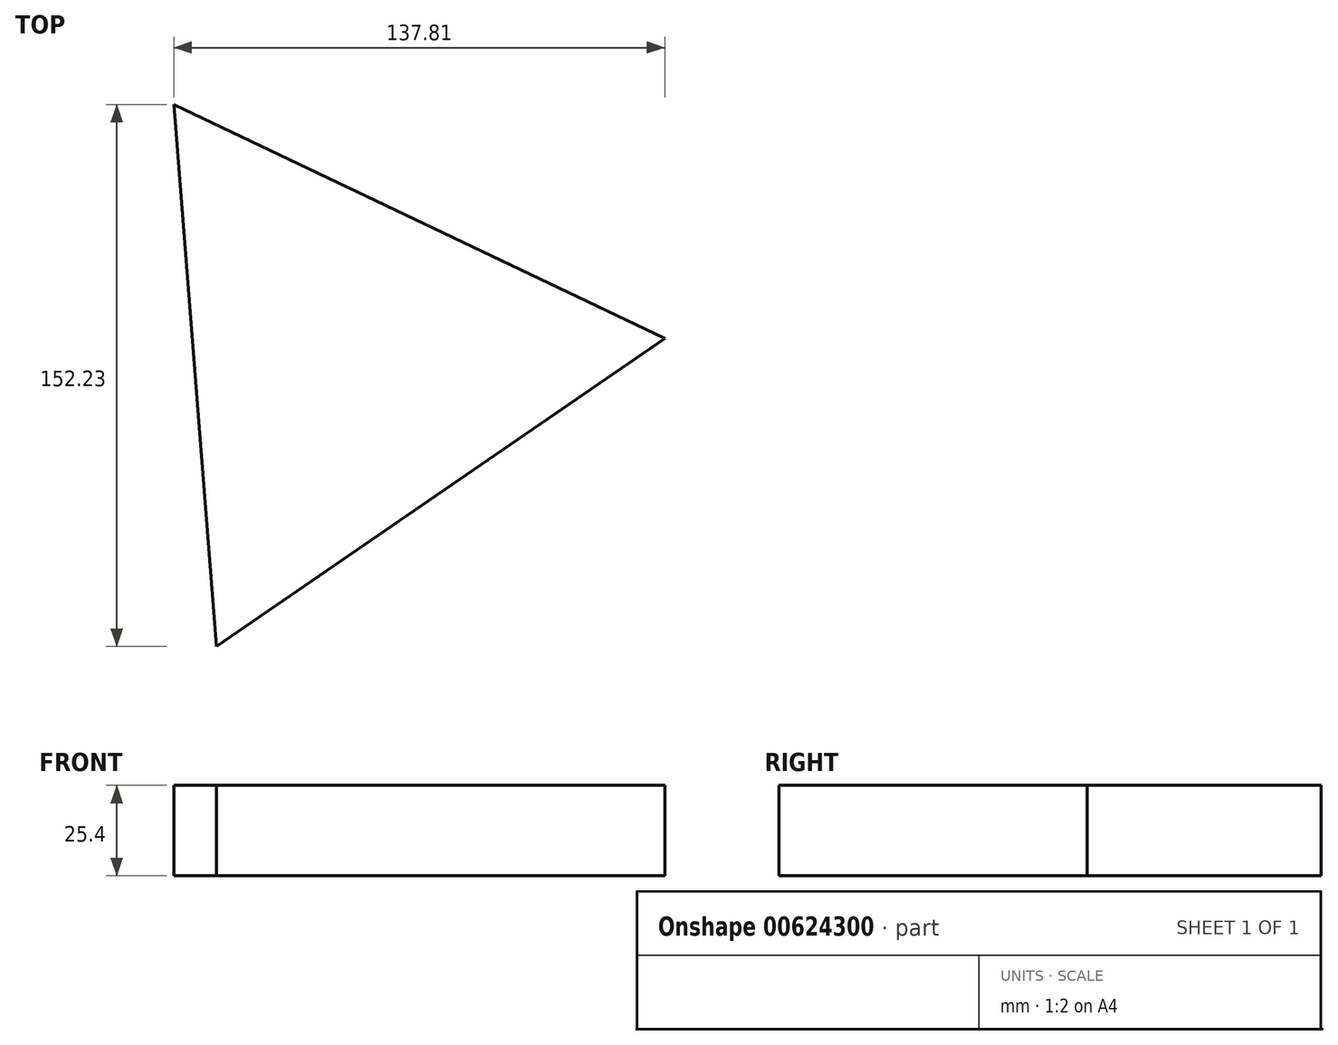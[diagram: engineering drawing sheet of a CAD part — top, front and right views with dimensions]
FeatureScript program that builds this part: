
annotation { "Feature Type Name" : "Feature", "Feature Type Description" : "" }
export const myFeature = defineFeature(function(context is Context, id is Id, definition is map)
    precondition{}
    {
        {
            var Q0;
            Q0=qCreatedBy(makeId("Top.planeOp"),FACE);
            var sketch = newSketch(context, id + "F0", { "sketchPlane" : qUnion([Q0])});
            skCircle(sketch, "E0.cCircle", {"center": v(0, 0) * mm, "radius": 44.08 * mm, "construction": true});
            skLineSegment(sketch, "E0.0", {"start": v(87.9, 6.9) * mm, "end": v(-37.97, -79.57) * mm});
            skLineSegment(sketch, "E0.1", {"start": v(-37.97, -79.57) * mm, "end": v(-49.92, 72.66) * mm});
            skLineSegment(sketch, "E0.2", {"start": v(-49.92, 72.66) * mm, "end": v(87.9, 6.9) * mm});
            skPoint(sketch, "E0.0.midPoint", {"position": v(24.96, -36.33) * mm});
            skSolve(sketch);
        }
        {
            var Q0;
            Q0 = qSketchRegion(id + "F0", true);
            extrude(context, id + "F1", {"entities" : qUnion([Q0]), "depth" : 25.4 * mm, "offsetDistance" : 25.4 * mm});
        }
    });
